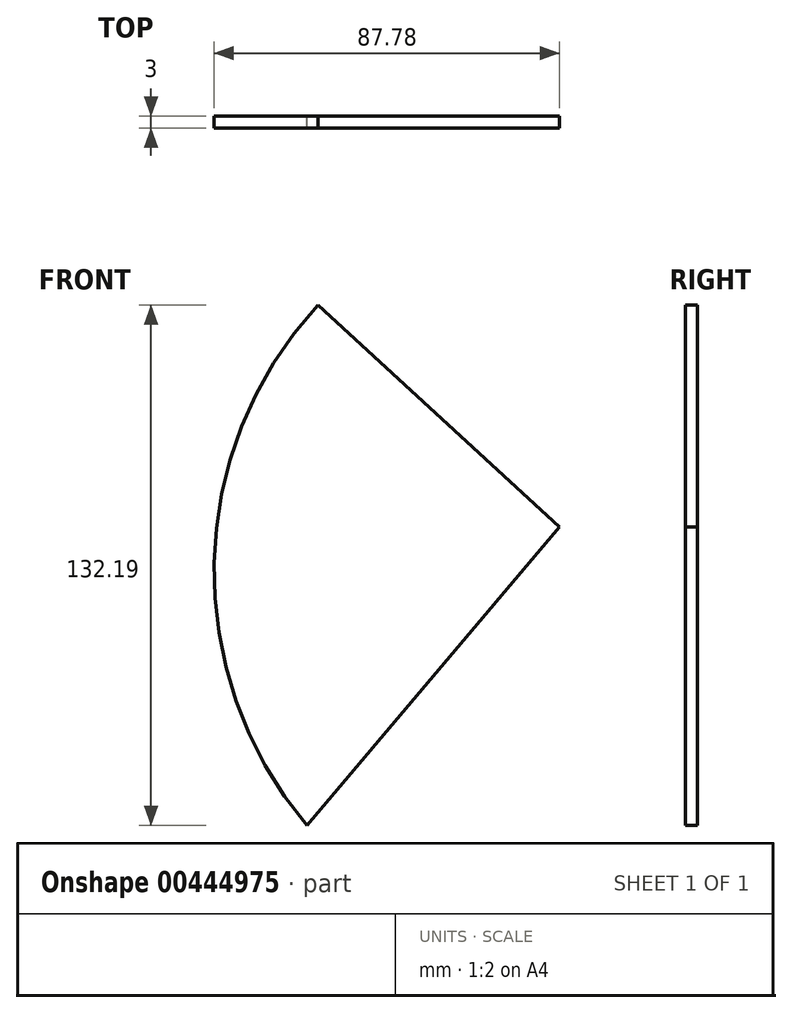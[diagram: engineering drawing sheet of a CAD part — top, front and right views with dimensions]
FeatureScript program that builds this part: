
annotation { "Feature Type Name" : "Feature", "Feature Type Description" : "" }
export const myFeature = defineFeature(function(context is Context, id is Id, definition is map)
    precondition{}
    {
        {
            var Q0;
            Q0=qCreatedBy(makeId("Front.planeOp"),FACE);
            var sketch = newSketch(context, id + "F0", { "sketchPlane" : qUnion([Q0])});
            skArc(sketch, "E0", {"start": v(-58.77, 99.34) * mm, "mid": v(-85.11, 33.77) * mm, "end": v(-61.53, -32.85) * mm});
            skLineSegment(sketch, "E1", {"start": v(2.64, 42.9) * mm, "end": v(-58.77, 99.34) * mm});
            skLineSegment(sketch, "E2", {"start": v(-61.53, -32.85) * mm, "end": v(2.64, 42.9) * mm});
            skSolve(sketch);
        }
        {
            var Q0;
            Q0=makeQuery(id+"F0.imprint","IMPRINT",FACE,{"disambiguationData":[TD([[makeQuery(id+"F0.imprint","IMPRINT",EDGE,{"derivedFrom":sQuery(id+"F0.wireOp",EDGE,"E0")}),1.0]])]});
            extrude(context, id + "F1", {"entities" : qUnion([Q0]), "depth" : 3 * mm});
        }
    });
